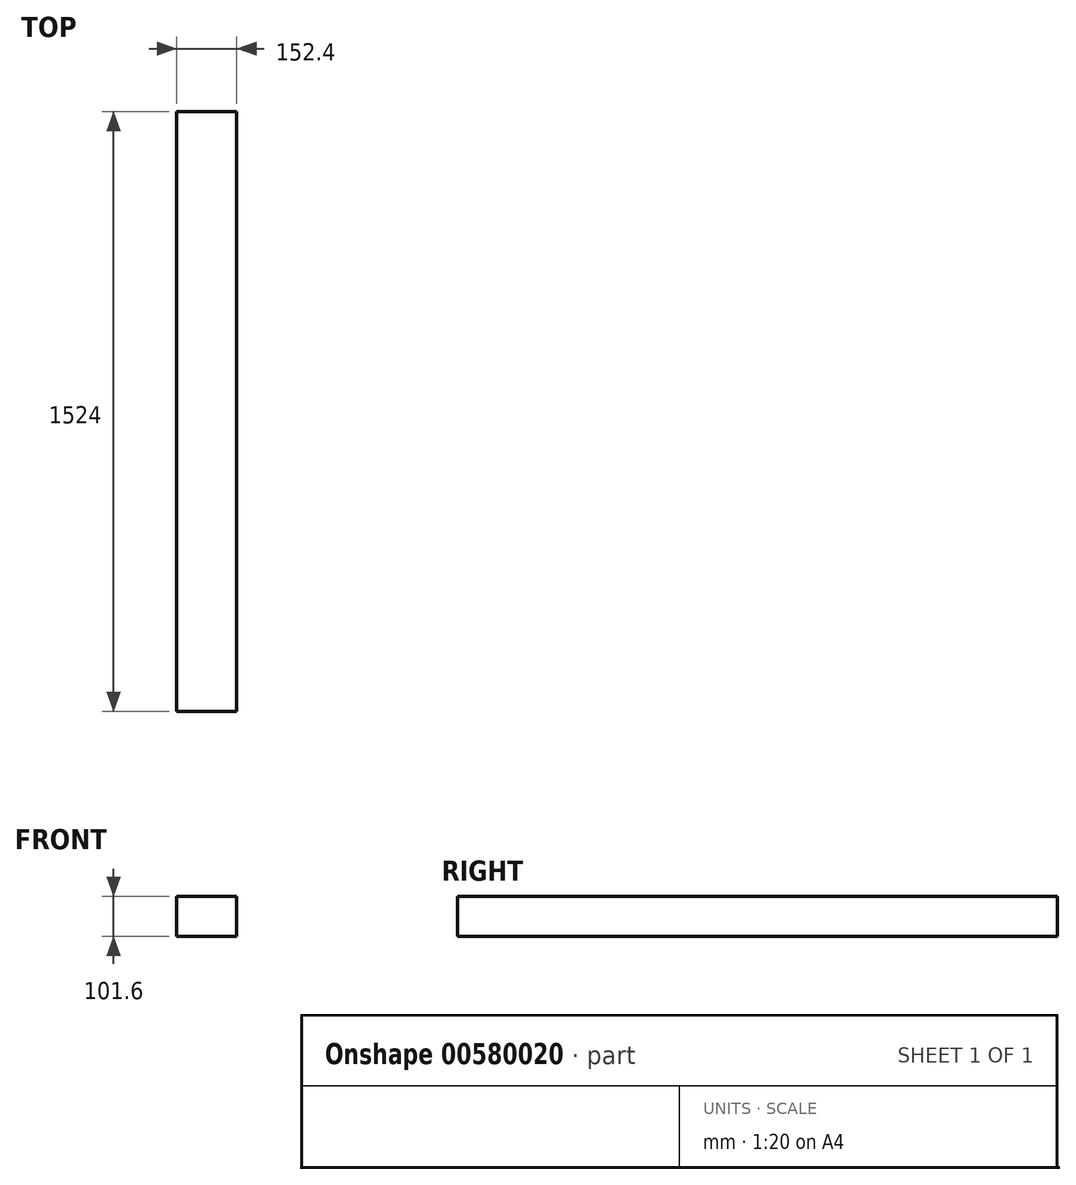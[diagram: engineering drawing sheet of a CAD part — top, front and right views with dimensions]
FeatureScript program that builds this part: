
annotation { "Feature Type Name" : "Feature", "Feature Type Description" : "" }
export const myFeature = defineFeature(function(context is Context, id is Id, definition is map)
    precondition{}
    {
        {
            var Q0;
            Q0=qCreatedBy(makeId("Front.planeOp"),FACE);
            var sketch = newSketch(context, id + "F0", { "sketchPlane" : qUnion([Q0])});
            skLineSegment(sketch, "E0.bottom", {"start": v(0, 0) * mm, "end": v(152.4, 0) * mm});
            skLineSegment(sketch, "E0.top", {"start": v(0, 101.6) * mm, "end": v(152.4, 101.6) * mm});
            skLineSegment(sketch, "E0.left", {"start": v(0, 0) * mm, "end": v(0, 101.6) * mm});
            skLineSegment(sketch, "E0.right", {"start": v(152.4, 0) * mm, "end": v(152.4, 101.6) * mm});
            skSolve(sketch);
        }
        {
            var Q0;
            Q0=makeQuery(id+"F0.imprint","IMPRINT",FACE,{"disambiguationData":[TD([[makeQuery(id+"F0.imprint","IMPRINT",EDGE,{"derivedFrom":sQuery(id+"F0.wireOp",EDGE,"E0.bottom")}),1.0]])]});
            extrude(context, id + "F1", {"entities" : qUnion([Q0]), "depth" : 1524 * mm, "offsetDistance" : 25.4 * mm});
        }
    });
